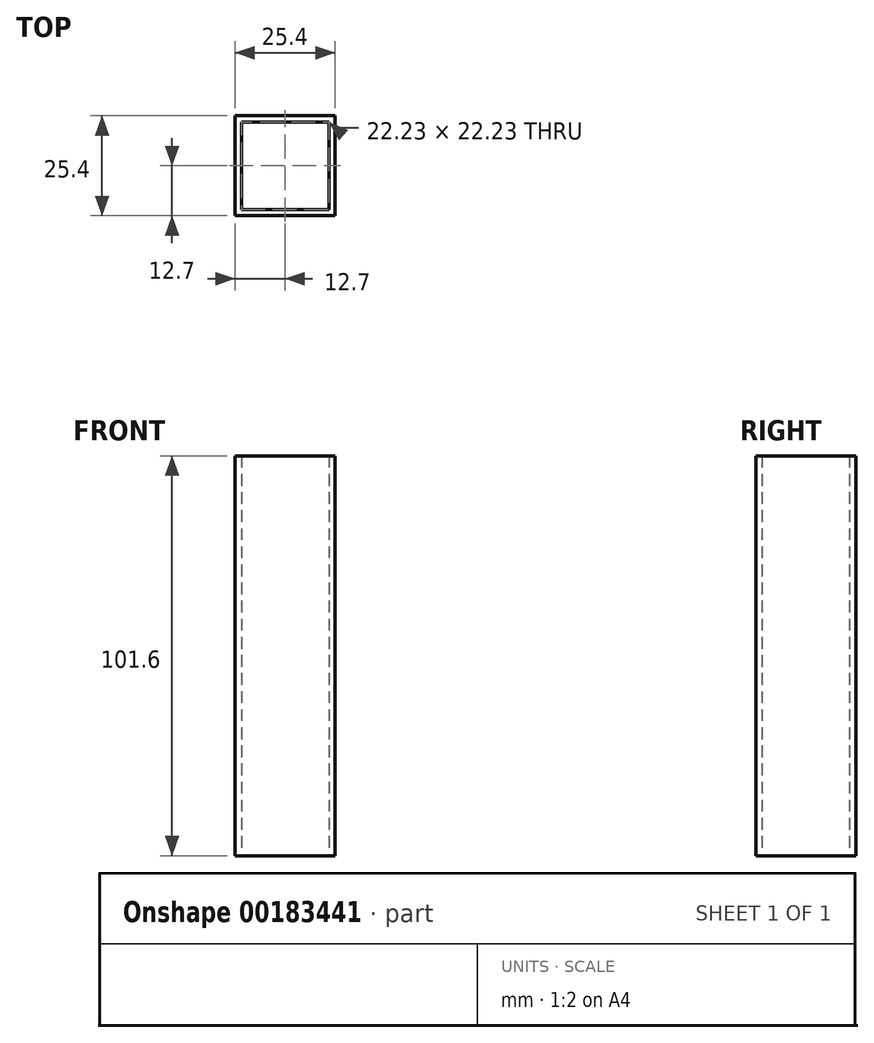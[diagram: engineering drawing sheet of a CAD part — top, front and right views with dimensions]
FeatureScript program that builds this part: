
annotation { "Feature Type Name" : "Feature", "Feature Type Description" : "" }
export const myFeature = defineFeature(function(context is Context, id is Id, definition is map)
    precondition{}
    {
        {
            var Q0;
            Q0=qCreatedBy(makeId("Top.planeOp"),FACE);
            var sketch = newSketch(context, id + "F0", { "sketchPlane" : qUnion([Q0])});
            skCircle(sketch, "E0.cCircle", {"center": v(0, 0) * mm, "radius": 12.7 * mm, "construction": true});
            skLineSegment(sketch, "E0.0", {"start": v(-12.7, 12.7) * mm, "end": v(12.7, 12.7) * mm});
            skLineSegment(sketch, "E0.1", {"start": v(12.7, 12.7) * mm, "end": v(12.7, -12.7) * mm});
            skLineSegment(sketch, "E0.2", {"start": v(12.7, -12.7) * mm, "end": v(-12.7, -12.7) * mm});
            skLineSegment(sketch, "E0.3", {"start": v(-12.7, -12.7) * mm, "end": v(-12.7, 12.7) * mm});
            skPoint(sketch, "E0.0.midPoint", {"position": v(0, 12.7) * mm});
            skCircle(sketch, "E1.cCircle", {"center": v(0, 0) * mm, "radius": 11.11 * mm, "construction": true});
            skLineSegment(sketch, "E1.0", {"start": v(-11.11, 11.11) * mm, "end": v(11.11, 11.11) * mm});
            skLineSegment(sketch, "E1.1", {"start": v(11.11, 11.11) * mm, "end": v(11.11, -11.11) * mm});
            skLineSegment(sketch, "E1.2", {"start": v(11.11, -11.11) * mm, "end": v(-11.11, -11.11) * mm});
            skLineSegment(sketch, "E1.3", {"start": v(-11.11, -11.11) * mm, "end": v(-11.11, 11.11) * mm});
            skPoint(sketch, "E1.0.midPoint", {"position": v(0, 11.11) * mm});
            skSolve(sketch);
        }
        {
            var Q0;
            Q0=makeQuery(id+"F0.imprint","IMPRINT",FACE,{"disambiguationData":[TD([[makeQuery(id+"F0.imprint","IMPRINT",EDGE,{"derivedFrom":sQuery(id+"F0.wireOp",EDGE,"E0.0")}),-1.0]])]});
            extrude(context, id + "F1", {"entities" : qUnion([Q0]), "depth" : 101.6 * mm});
        }
    });
